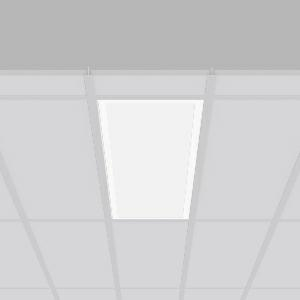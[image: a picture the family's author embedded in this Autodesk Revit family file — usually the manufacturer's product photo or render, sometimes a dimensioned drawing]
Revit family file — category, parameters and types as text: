
# Revit family: sidelite_eco_672377_002_7c3b
name_source: partatom
category: Lighting Fixtures
units: mm (PartAtom-declared; Revit-internal decimal feet)

## family parameters
Cut with Voids When Loaded = No
Host = Face
Light Source = No
Part Type = Normal
Room Calculation Point = No
Round Connector Dimension = Use Diameter
Shared = No

## types (1)
- SIDELITE ECO (1 x LED Modul 830, 3300 lm, 3000)
    Apparent Load = 29 VA
    CIE Flux Codes = 47 79 96 100 100
    Color Rendering = 80
    Color Temperature = 3000
    Default Elevation = 1800 mm
    Description = Series: SIDELITE ECO
Highly economical recessed luminaire with progressive LED technology. For escape route illumination. Frame made of aluminium, powder-coated. Diffuser: plastic, opal. Lightguide and diffuser made of non-yellowing plastic (PMMA). Lateral light emission (RZB SIDELITE technology) for homogeneous light distribution. External driver. Self-contained system with automatic self-test. External driver with simple plug-in locking system. Extended connection cable (1.90 m). 
Colour: white
Length: 1245 mm
Width: 308 mm
Cut-out length: 1220 mm
Cut-out width: 285 mm
Recess height: 160 mm
Luminaire: recess height: 40 mm
Weight: 4.7 kg
Operating mode: maintained power mode
Duration time: 3 h
Lamp: LED
Socket: without socket
Colour temperature: 3000K
Colour rendering index (CRI): 80
System power: 29 W
Rated luminous flux: 3300 lm
Luminous flux, emergency: 480 lm
System power, emergency: -
Control gear: Regulated power supply
Protection class: I
Type of protection: IP 40
    Height = 0 mm  [stored 0 ft]
    Lamp = 1 x LED Modul 830
    Lamp Light Flux = 3300 lm
    Lamp count = 1
    Length = 1245 mm
    Lifetime = 50000 h
    Luminous efficacy = 114 lm/W
    Manufacturer = RZB
    ModVariant = No
    Model = 672377.002
    Mounting Place = Ceiling
    Mounting Type = Recessed
    Number of Poles = 1
    OnlyDefault = Yes
    Power Factor = 1
    Product Name = SIDELITE ECO
    Product group = Recessed modular luminaires
    ProductGroupID = 406
    Protection Class = Protection class I
    Protection Degree = IP 40
    RLX_Detail_Level = 1
    RLX_Emergency_Light_Flux = 480 lm
    RLX_Emergency_Type = 3
    RLX_Emergency_Type_DB = Yes
    RlxData = <blob elided: 30093 chars, md5=a34f16a2>
    Socket = socket
    Standby Power = 0 W
    System Light Flux = 3300 lm
    System Power = 29 W
    Type Comments = Product without accessories
    Type Image = 312367.002.jpg
    URL = http://relux.com
    VarID = ---
    Voltage = 230 V
    Voltage Range = 220-240 V
    Weight = 0.00 kg
    Width = 308 mm

note: [stored X ft] marks values corroborated as IEEE doubles in the binary element streams (Revit-internal decimal feet)

## geometry (parser evidence)
native form markers: Blend x4, Sweep x12
no freeform markers — native parametric forms only
